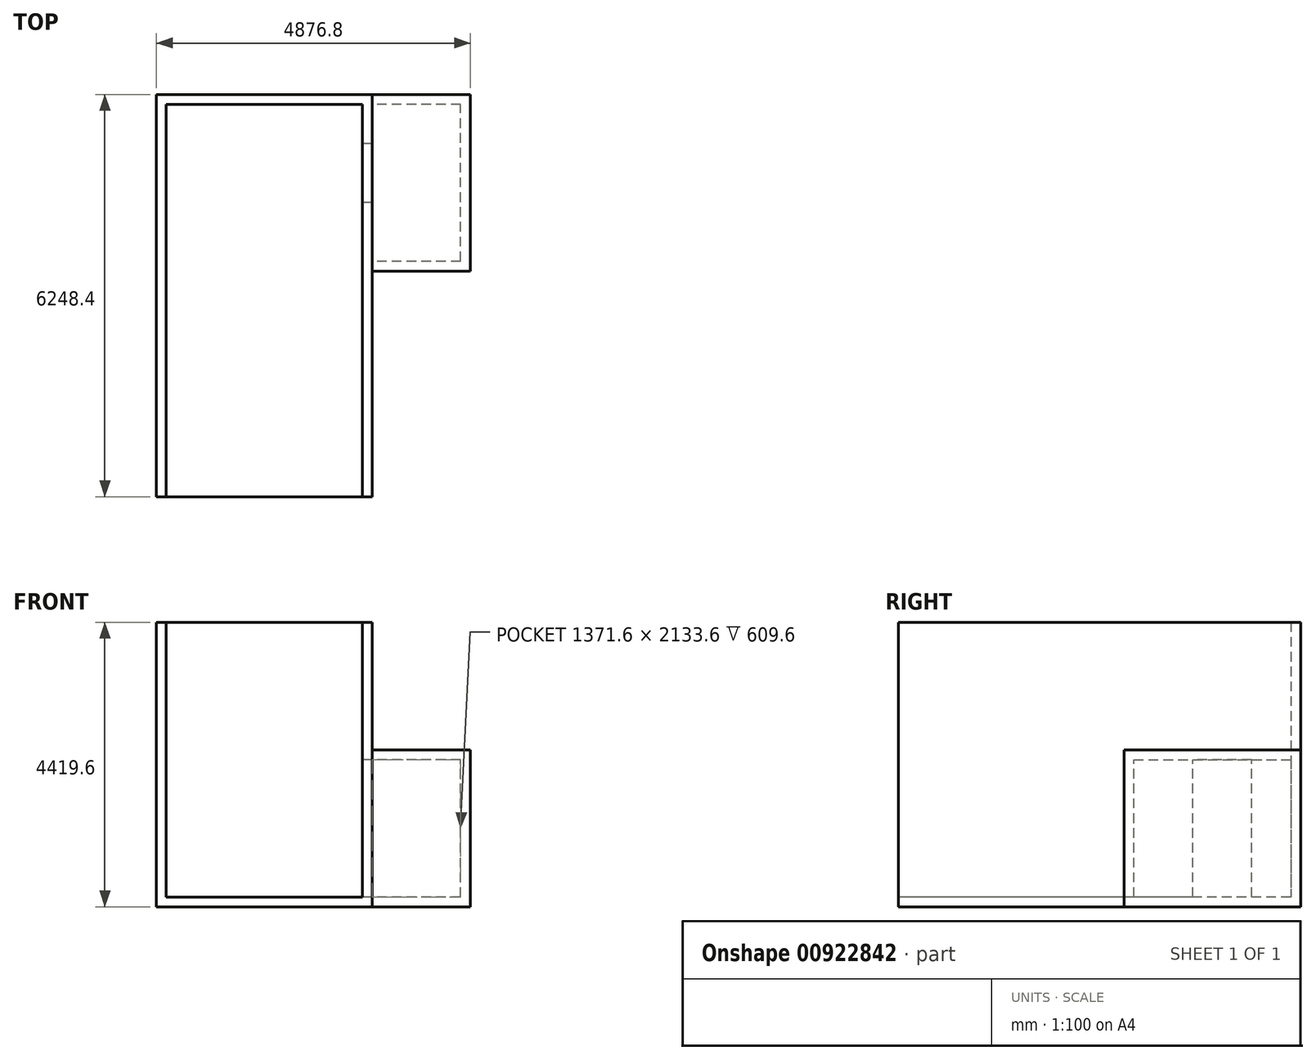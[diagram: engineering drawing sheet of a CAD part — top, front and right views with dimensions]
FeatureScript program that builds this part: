
annotation { "Feature Type Name" : "Feature", "Feature Type Description" : "" }
export const myFeature = defineFeature(function(context is Context, id is Id, definition is map)
    precondition{}
    {
        {
            var Q0;
            Q0=qCreatedBy(makeId("Top.planeOp"),FACE);
            var sketch = newSketch(context, id + "F0", { "sketchPlane" : qUnion([Q0])});
            skLineSegment(sketch, "E0.bottom", {"start": v(0, 0) * mm, "end": v(-3048, 0) * mm});
            skLineSegment(sketch, "E0.top", {"start": v(0, -6096) * mm, "end": v(-3048, -6096) * mm});
            skLineSegment(sketch, "E0.left", {"start": v(0, 0) * mm, "end": v(0, -6096) * mm});
            skLineSegment(sketch, "E0.right", {"start": v(-3048, 0) * mm, "end": v(-3048, -6096) * mm});
            skSolve(sketch);
        }
        {
            var Q0;
            Q0=makeQuery(id+"F0.imprint","IMPRINT",FACE,{"disambiguationData":[TD([[makeQuery(id+"F0.imprint","IMPRINT",EDGE,{"derivedFrom":sQuery(id+"F0.wireOp",EDGE,"E0.bottom")}),1.0]])]});
            extrude(context, id + "F1", {"entities" : qUnion([Q0]), "depth" : 4267.2 * mm, "offsetDistance" : 30.48 * mm});
        }
        {
            var Q0;
            Q0=makeQuery(id+"F1.opExtrude","CAP_FACE",FACE,{"disambiguationData":[OSD([sQuery(id+"F0.wireOp",EDGE,"E0.bottom"),sQuery(id+"F0.wireOp",EDGE,"E0.top"),sQuery(id+"F0.wireOp",EDGE,"E0.left"),sQuery(id+"F0.wireOp",EDGE,"E0.right")])],"isStart":false});
            var Q1;
            Q1=makeQuery(id+"F1.opExtrude","SWEPT_FACE",FACE,{"disambiguationData":[OSD([sQuery(id+"F0.wireOp",EDGE,"E0.top")])]});
            shell(context, id + "F2", {"entities" : qUnion([Q0, Q1]), "thickness" : 152.4 * mm, "oppositeDirection" : true});
        }
        {
            var Q0;
            Q0=makeQuery(id+"F2.opShell","OFFSET_FACE",FACE,{"disambiguationData":[OSD([sQuery(id+"F0.wireOp",EDGE,"E0.left")])]});
            var sketch = newSketch(context, id + "F3", { "sketchPlane" : qUnion([Q0])});
            skLineSegment(sketch, "E1.bottom", {"start": v(2438.4, 0) * mm, "end": v(0, 0) * mm});
            skLineSegment(sketch, "E1.top", {"start": v(2438.4, 2133.6) * mm, "end": v(0, 2133.6) * mm});
            skLineSegment(sketch, "E1.left", {"start": v(2438.4, 0) * mm, "end": v(2438.4, 2133.6) * mm});
            skLineSegment(sketch, "E1.right", {"start": v(0, 0) * mm, "end": v(0, 2133.6) * mm});
            skSolve(sketch);
        }
        {
            var Q0;
            Q0 = qSketchRegion(id + "F3", true);
            extrude(context, id + "F4", {"entities" : qUnion([Q0]), "oppositeDirection" : true, "depth" : 1524 * mm, "offsetDistance" : 30.48 * mm});
        }
        {
            var Q0;
            Q0=makeQuery(id+"F4.opExtrude","CAP_FACE",FACE,{"disambiguationData":[OSD([sQuery(id+"F3.wireOp",EDGE,"E1.bottom"),sQuery(id+"F3.wireOp",EDGE,"E1.top"),sQuery(id+"F3.wireOp",EDGE,"E1.left"),sQuery(id+"F3.wireOp",EDGE,"E1.right")])],"isStart":true});
            shell(context, id + "F5", {"entities" : qUnion([Q0]), "thickness" : 152.4 * mm, "oppositeDirection" : true});
        }
        {
            var Q0;
            Q0=makeQuery(id+"F4.opExtrude","SWEPT_BODY",BODY,{"disambiguationData":[OSD([sQuery(id+"F3.wireOp",EDGE,"E1.bottom"),sQuery(id+"F3.wireOp",EDGE,"E1.top"),sQuery(id+"F3.wireOp",EDGE,"E1.left"),sQuery(id+"F3.wireOp",EDGE,"E1.right")])]});
            var Q1;
            Q1=makeQuery(id+"F1.opExtrude","SWEPT_BODY",BODY,{"disambiguationData":[OSD([sQuery(id+"F0.wireOp",EDGE,"E0.bottom"),sQuery(id+"F0.wireOp",EDGE,"E0.top"),sQuery(id+"F0.wireOp",EDGE,"E0.left"),sQuery(id+"F0.wireOp",EDGE,"E0.right")])]});
            booleanBodies(context, id + "F6", {"operationType" : BooleanOperationType.UNION, "tools" : qUnion([Q0, Q1])});
        }
        {
            var Q0;
            Q0=makeQuery(id+"F6.opBoolean","MERGE",FACE,{"derivedFrom":[makeQuery(id+"F2.opShell","OFFSET_FACE",FACE,{"disambiguationData":[OSD([sQuery(id+"F0.wireOp",EDGE,"E0.left")])]}),makeQuery(id+"F4.opExtrude","CAP_FACE",FACE,{"disambiguationData":[OSD([sQuery(id+"F3.wireOp",EDGE,"E1.bottom"),sQuery(id+"F3.wireOp",EDGE,"E1.top"),sQuery(id+"F3.wireOp",EDGE,"E1.left"),sQuery(id+"F3.wireOp",EDGE,"E1.right")])],"isStart":true})]});
            var sketch = newSketch(context, id + "F7", { "sketchPlane" : qUnion([Q0])});
            skLineSegment(sketch, "E2.bottom", {"start": v(609.6, 0) * mm, "end": v(1524, 0) * mm});
            skLineSegment(sketch, "E2.top", {"start": v(609.6, 2133.6) * mm, "end": v(1524, 2133.6) * mm});
            skLineSegment(sketch, "E2.left", {"start": v(609.6, 0) * mm, "end": v(609.6, 2133.6) * mm});
            skLineSegment(sketch, "E2.right", {"start": v(1524, 0) * mm, "end": v(1524, 2133.6) * mm});
            skSolve(sketch);
        }
        {
            var Q0;
            Q0 = qSketchRegion(id + "F7", true);
            extrude(context, id + "F8", {"entities" : qUnion([Q0]), "operationType" : NewBodyOperationType.REMOVE, "oppositeDirection" : true, "depth" : 152.4 * mm, "offsetDistance" : 30.48 * mm});
        }
    });
